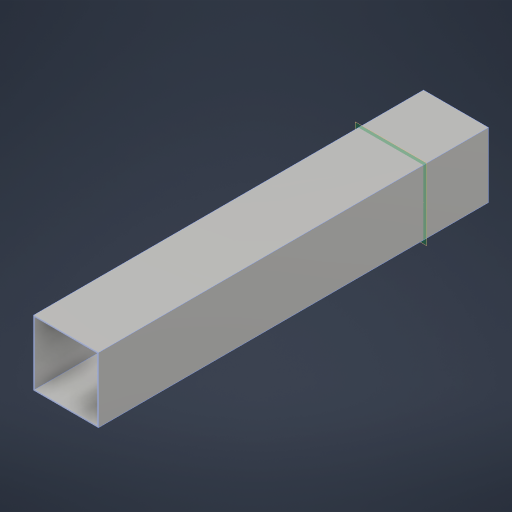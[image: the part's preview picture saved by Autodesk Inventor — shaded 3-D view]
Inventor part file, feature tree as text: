
AUTODESK INVENTOR PART (.ipt)
format: ipt  version: 2024.2 (Build 282272000, 272)  size: 173,056 bytes
history: native  units: in
note: dims shown in document units (in); Inventor stores cm internally (conversion verified against a paired STEP export)
features: extrude x1, other x1, plane x1
ambient origin geometry x8: Origin, YZ Plane, XZ Plane, XY Plane, X Axis, Y Axis, Z Axis, Center Point
bodies: Solid1 (feature_tree)
feature tree (3):
  extrude  "Extrusion1"  TaperAngle=0.0deg  [1 undecoded]
  other  "Work Axis1"
  plane  "Work Plane1"
note: 1 required parameter value undecoded (feature->parameter linkage not recoverable at this tier; creation-order binding heuristic only, values carry confidence <= 0.55)
